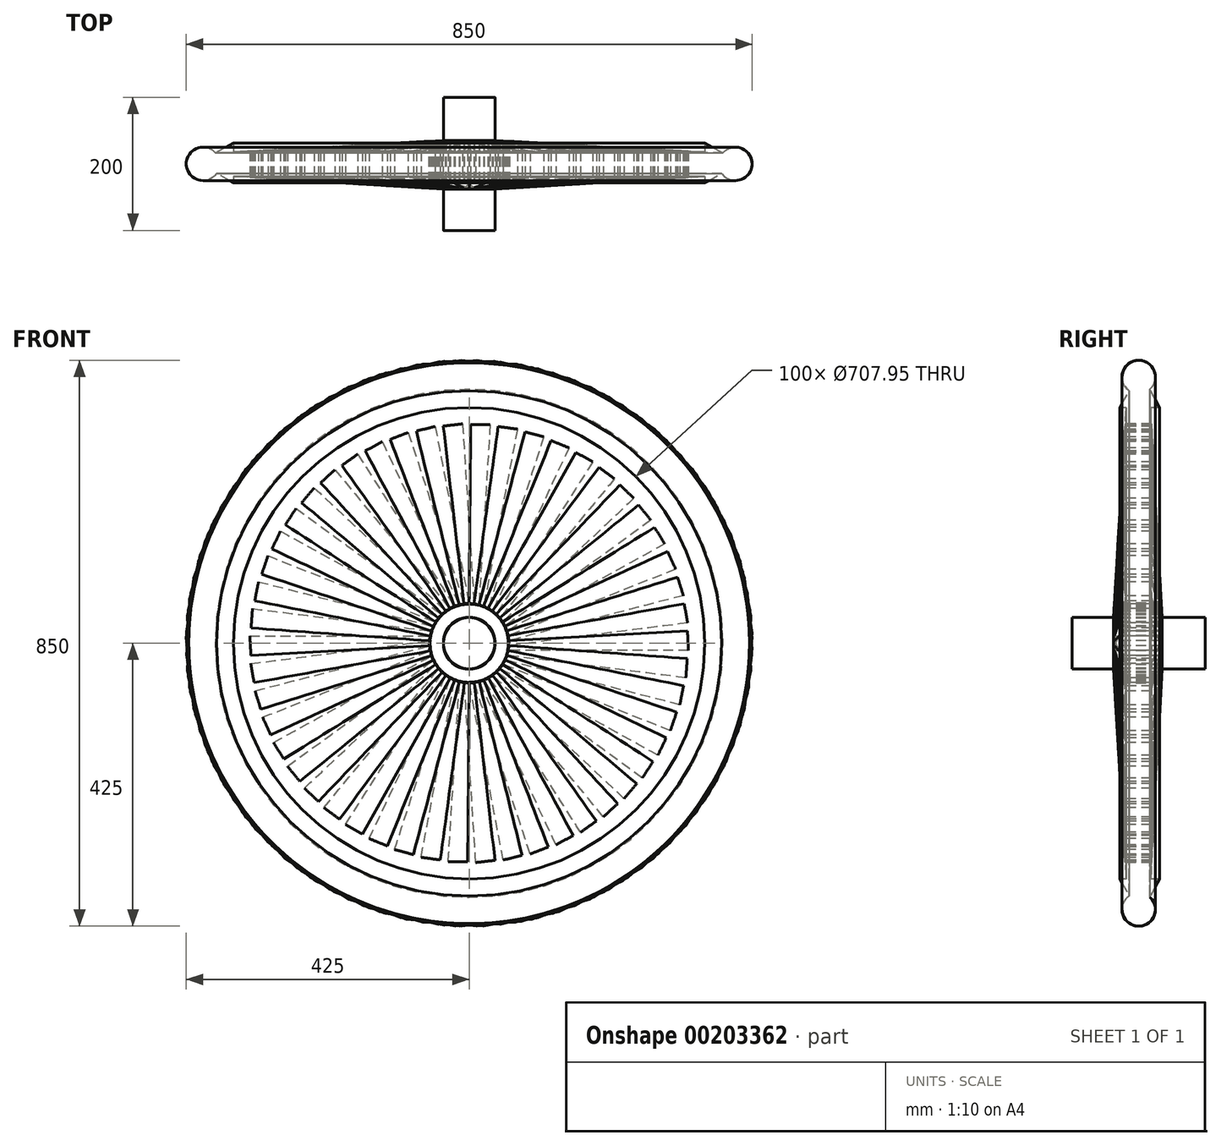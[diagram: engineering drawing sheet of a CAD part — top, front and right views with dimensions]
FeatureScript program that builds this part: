
annotation { "Feature Type Name" : "Feature", "Feature Type Description" : "" }
export const myFeature = defineFeature(function(context is Context, id is Id, definition is map)
    precondition{}
    {
        {
            var Q0;
            Q0=qCreatedBy(makeId("Top.planeOp"),FACE);
            var sketch = newSketch(context, id + "F0", { "sketchPlane" : qUnion([Q0])});
            skCircle(sketch, "E0", {"center": v(400, 0) * mm, "radius": 25 * mm});
            skLineSegment(sketch, "E1", {"start": v(0, 0) * mm, "end": v(0, 44.8) * mm});
            skLineSegment(sketch, "E2", {"start": v(379.47, -14.26) * mm, "end": v(353.98, -28.3) * mm});
            skLineSegment(sketch, "E3", {"start": v(353.98, -28.3) * mm, "end": v(353.98, 31.07) * mm});
            skLineSegment(sketch, "E4", {"start": v(353.98, 31.07) * mm, "end": v(381.4, 16.71) * mm});
            skLineSegment(sketch, "E5", {"start": v(353.98, -18.87) * mm, "end": v(0, -39.96) * mm});
            skLineSegment(sketch, "E6", {"start": v(0, -39.96) * mm, "end": v(0, 37.18) * mm});
            skLineSegment(sketch, "E7", {"start": v(0, 37.18) * mm, "end": v(353.98, 17.75) * mm});
            skSolve(sketch);
        }
        {
            var Q0;
            Q0=makeQuery(id+"F0.imprint","IMPRINT",FACE,{"disambiguationData":[TD([[makeQuery(id+"F0.imprint","IMPRINT",EDGE,{"derivedFrom":sQuery(id+"F0.wireOp",EDGE,"E0")}),1.0]])]});
            var Q1;
            {var subQ3=sQuery(id+"F0.wireOp",EDGE,"E2");Q1=makeQuery(id+"F0.imprint","IMPRINT",FACE,{"disambiguationData":[TD([[makeQuery(id+"F0.imprint","IMPRINT",EDGE,{"derivedFrom":subQ3}),-1.0]])]});}
            var Q2;
            {var subQ0=sQuery(id+"F0.wireOp",EDGE,"E5");Q2=makeQuery(id+"F0.imprint","IMPRINT",FACE,{"disambiguationData":[TD([[makeQuery(id+"F0.imprint","IMPRINT",EDGE,{"derivedFrom":subQ0}),-1.0]])]});}
            var Q3;
            Q3=sQuery(id+"F0.wireOp",EDGE,"E1");
            revolve(context, id + "F1", {"surfaceOperationType" : NewSurfaceOperationType.NEW, "entities" : qUnion([Q0, Q1, Q2]), "axis" : qUnion([Q3]), "revolveType" : RevolveType.ONE_DIRECTION, "angle" : 360 * degree});
        }
        {
            var Q0;
            Q0=qCreatedBy(makeId("Front.planeOp"),FACE);
            var sketch = newSketch(context, id + "F2", { "sketchPlane" : qUnion([Q0])});
            skCircle(sketch, "E8", {"center": v(0, 0) * mm, "radius": 38.74 * mm});
            skSolve(sketch);
        }
        {
            var Q0;
            Q0 = qSketchRegion(id + "F2", true);
            extrude(context, id + "F3", {"entities" : qUnion([Q0]), "operationType" : NewBodyOperationType.ADD, "depth" : 100 * mm, "offsetDistance" : 25 * mm, "hasSecondDirection" : true, "secondDirectionOppositeDirection" : true, "secondDirectionDepth" : 100 * mm});
        }
        {
            var Q0;
            Q0=qCreatedBy(makeId("Front.planeOp"),FACE);
            var sketch = newSketch(context, id + "F4", { "sketchPlane" : qUnion([Q0])});
            skLineSegment(sketch, "E9", {"start": v(-15.25, 58.6) * mm, "end": v(-79.46, 318.64) * mm});
            skLineSegment(sketch, "E10", {"start": v(-79.46, 318.64) * mm, "end": v(-51.12, 325.63) * mm});
            skLineSegment(sketch, "E11", {"start": v(-51.12, 325.63) * mm, "end": v(0, 58.6) * mm});
            skLineSegment(sketch, "E12", {"start": v(0, 58.6) * mm, "end": v(-15.25, 58.6) * mm});
            skSolve(sketch);
        }
        {
            var Q0;
            Q0 = qSketchRegion(id + "F4", true);
            extrude(context, id + "F5", {"entities" : qUnion([Q0]), "operationType" : NewBodyOperationType.REMOVE, "endBound" : BoundingType.THROUGH_ALL, "oppositeDirection" : true, "depth" : 25 * mm, "offsetDistance" : 25 * mm, "hasSecondDirection" : true, "secondDirectionOppositeDirection" : false, "secondDirectionDepth" : 100 * mm});
        }
        {
            var Q0;
            Q0=makeQuery(id+"F1.opRevolve","SWEPT_BODY",BODY,{"disambiguationData":[OSD([sQuery(id+"F0.wireOp",EDGE,"E0"),sQuery(id+"F0.wireOp",EDGE,"E2"),sQuery(id+"F0.wireOp",EDGE,"E3"),sQuery(id+"F0.wireOp",EDGE,"E4"),sQuery(id+"F0.wireOp",EDGE,"E5"),sQuery(id+"F0.wireOp",EDGE,"E6"),sQuery(id+"F0.wireOp",EDGE,"E7")])]});
            var Q1;
            {var subQ0=sQuery(id+"F2.wireOp",EDGE,"E8");Q1=makeQuery(id+"F3.boolean.opBoolean","SPLIT",FACE,{"disambiguationData":[TD([makeQuery(id+"F1.opRevolve","SWEPT_FACE",FACE,{"disambiguationData":[OSD([sQuery(id+"F0.wireOp",EDGE,"E7")])]})])],"derivedFrom":makeQuery(id+"F3.opExtrude","SWEPT_FACE",FACE,{"disambiguationData":[OSD([subQ0])]})});}
            circularPattern(context, id + "F6", {"entities" : qUnion([Q0]), "axis" : qUnion([Q1]), "angle" : 360 * degree, "instanceCount" : 50, "equalSpace" : true});
        }
    });
